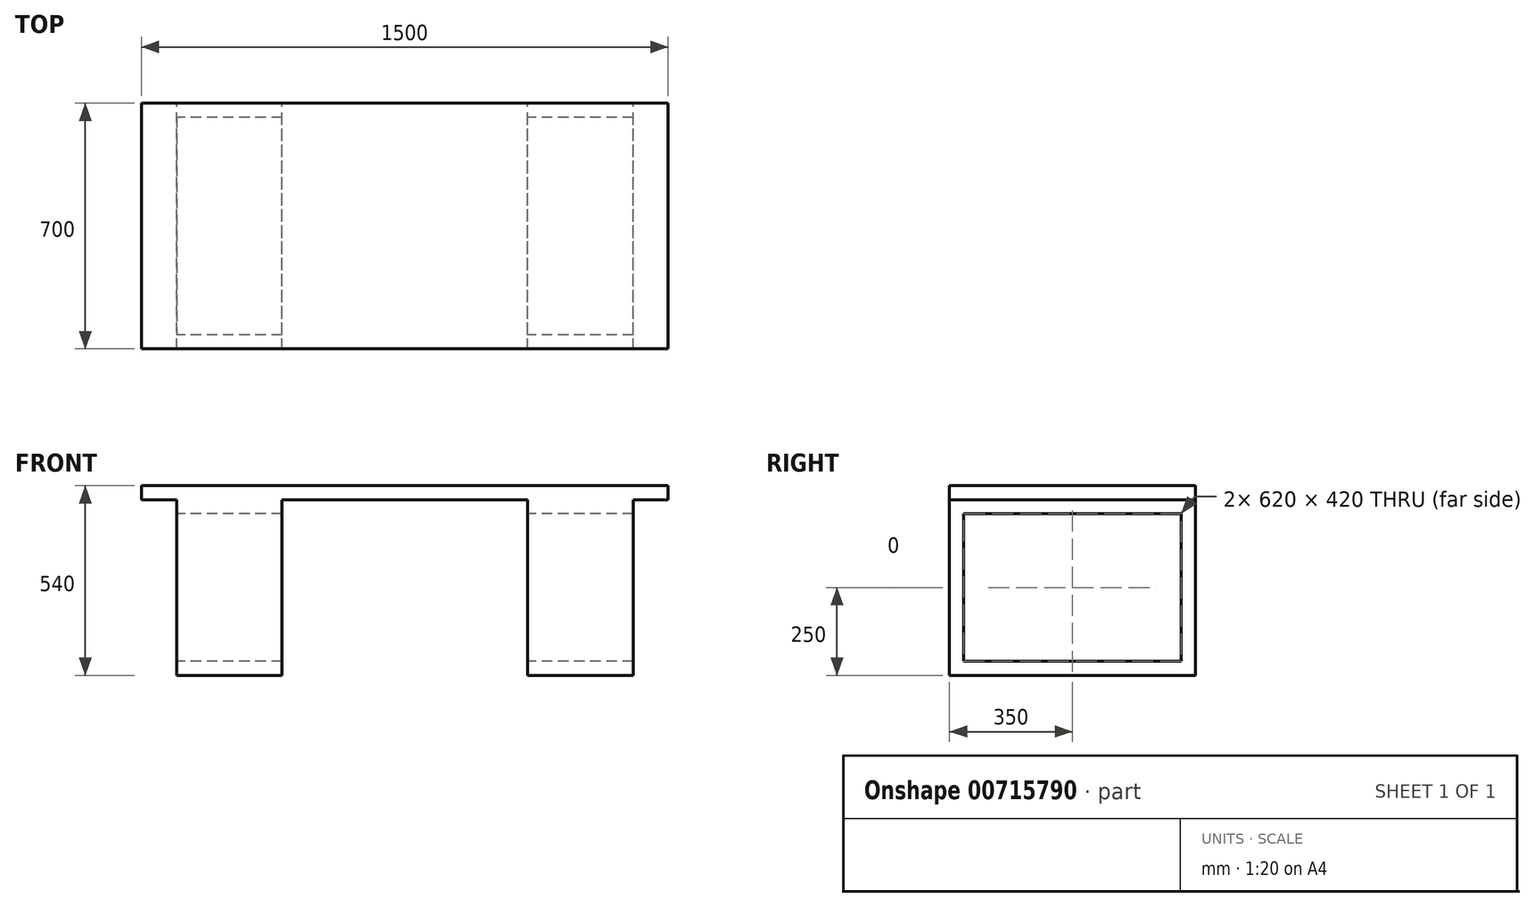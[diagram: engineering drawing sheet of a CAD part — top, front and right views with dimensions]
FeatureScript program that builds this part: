
annotation { "Feature Type Name" : "Feature", "Feature Type Description" : "" }
export const myFeature = defineFeature(function(context is Context, id is Id, definition is map)
    precondition{}
    {
        {
            var Q0;
            Q0=qCreatedBy(makeId("Top.planeOp"),FACE);
            var sketch = newSketch(context, id + "F0", { "sketchPlane" : qUnion([Q0])});
            skLineSegment(sketch, "E0.bottom", {"start": v(0, 0) * mm, "end": v(1500, 0) * mm});
            skLineSegment(sketch, "E0.top", {"start": v(0, -700) * mm, "end": v(1500, -700) * mm});
            skLineSegment(sketch, "E0.left", {"start": v(0, 0) * mm, "end": v(0, -700) * mm});
            skLineSegment(sketch, "E0.right", {"start": v(1500, 0) * mm, "end": v(1500, -700) * mm});
            skSolve(sketch);
        }
        {
            var Q0;
            Q0=makeQuery(id+"F0.imprint","IMPRINT",FACE,{"disambiguationData":[TD([[makeQuery(id+"F0.imprint","IMPRINT",EDGE,{"derivedFrom":sQuery(id+"F0.wireOp",EDGE,"E0.bottom")}),-1.0]])]});
            extrude(context, id + "F1", {"entities" : qUnion([Q0]), "oppositeDirection" : true, "depth" : 40 * mm, "offsetDistance" : 25 * mm});
        }
        {
            var Q0;
            Q0=makeQuery(id+"F1.opExtrude","CAP_FACE",FACE,{"disambiguationData":[OSD([sQuery(id+"F0.wireOp",EDGE,"E0.bottom"),sQuery(id+"F0.wireOp",EDGE,"E0.top"),sQuery(id+"F0.wireOp",EDGE,"E0.left"),sQuery(id+"F0.wireOp",EDGE,"E0.right")])],"isStart":false});
            var sketch = newSketch(context, id + "F2", { "sketchPlane" : qUnion([Q0])});
            skLineSegment(sketch, "E1.bottom", {"start": v(100, 700) * mm, "end": v(400, 700) * mm});
            skLineSegment(sketch, "E1.top", {"start": v(100, 0) * mm, "end": v(400, 0) * mm});
            skLineSegment(sketch, "E1.left", {"start": v(100, 700) * mm, "end": v(100, 0) * mm});
            skLineSegment(sketch, "E1.right", {"start": v(400, 700) * mm, "end": v(400, 0) * mm});
            skLineSegment(sketch, "E2.bottom", {"start": v(1100, 700) * mm, "end": v(1400, 700) * mm});
            skLineSegment(sketch, "E2.top", {"start": v(1100, 0) * mm, "end": v(1400, 0) * mm});
            skLineSegment(sketch, "E2.left", {"start": v(1100, 700) * mm, "end": v(1100, 0) * mm});
            skLineSegment(sketch, "E2.right", {"start": v(1400, 700) * mm, "end": v(1400, 0) * mm});
            skSolve(sketch);
        }
        {
            var Q0;
            Q0=qSketchRegion(id+"F2",true);
            extrude(context, id + "F3", {"entities" : qUnion([Q0]), "operationType" : NewBodyOperationType.ADD, "depth" : 500 * mm, "offsetDistance" : 25 * mm});
        }
        {
            var Q0;
            Q0=makeQuery(id+"F3.opExtrude","SWEPT_FACE",FACE,{"disambiguationData":[OSD([sQuery(id+"F2.wireOp",EDGE,"E1.left")])]});
            var sketch = newSketch(context, id + "F4", { "sketchPlane" : qUnion([Q0])});
            skLineSegment(sketch, "E3.bottom", {"start": v(40, -80) * mm, "end": v(660, -80) * mm});
            skLineSegment(sketch, "E3.top", {"start": v(40, -500) * mm, "end": v(660, -500) * mm});
            skLineSegment(sketch, "E3.left", {"start": v(40, -80) * mm, "end": v(40, -500) * mm});
            skLineSegment(sketch, "E3.right", {"start": v(660, -80) * mm, "end": v(660, -500) * mm});
            skSolve(sketch);
        }
        {
            var Q0;
            Q0=qSketchRegion(id+"F4",true);
            extrude(context, id + "F5", {"entities" : qUnion([Q0]), "operationType" : NewBodyOperationType.REMOVE, "oppositeDirection" : true, "depth" : 1328 * mm, "offsetDistance" : 25 * mm});
        }
    });
